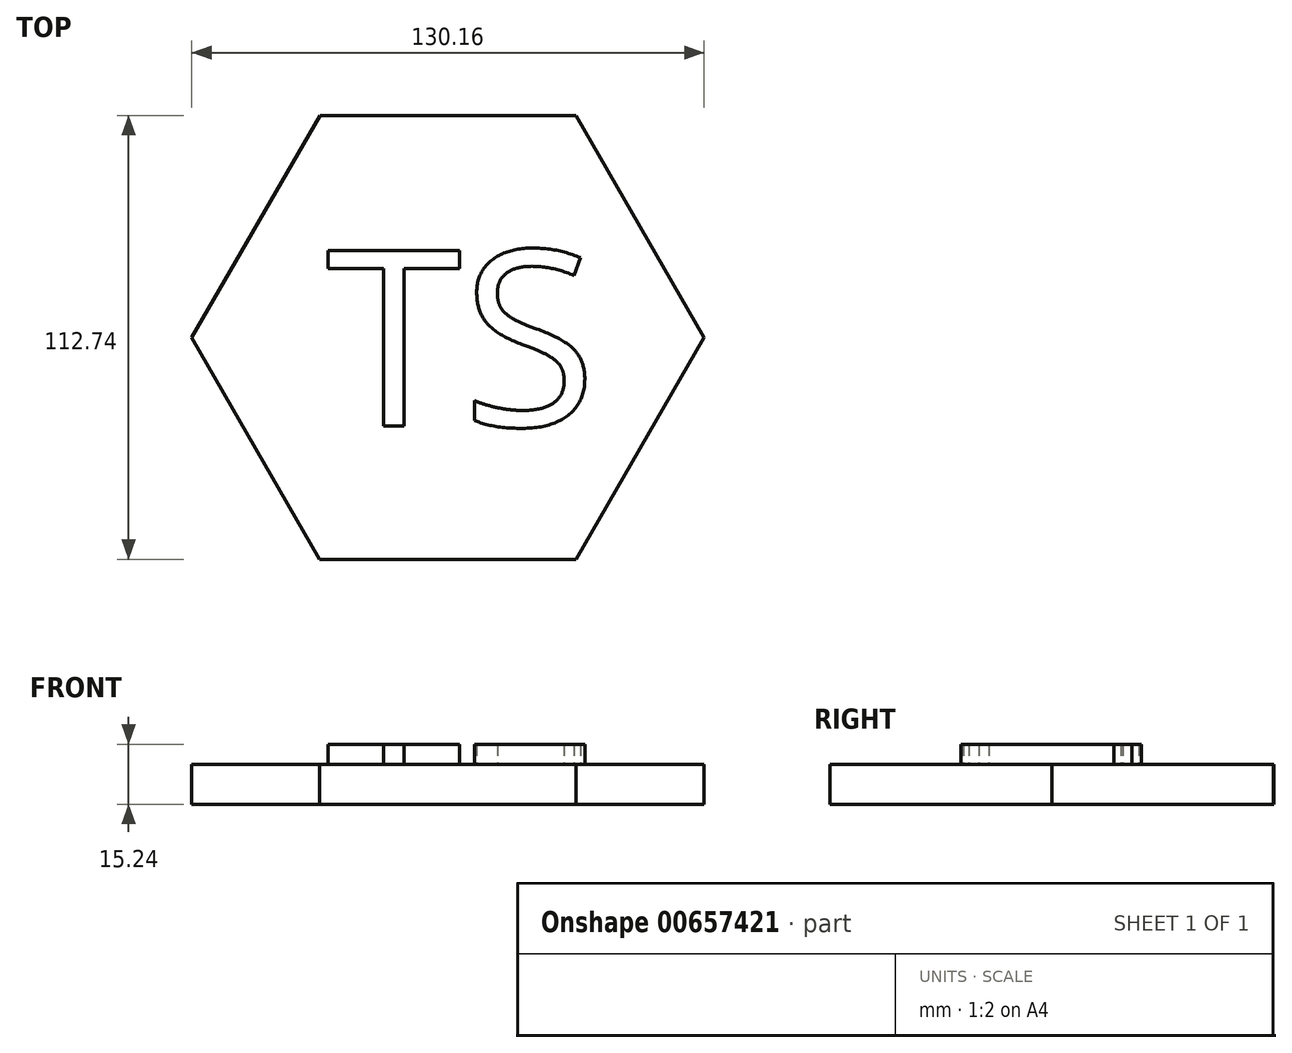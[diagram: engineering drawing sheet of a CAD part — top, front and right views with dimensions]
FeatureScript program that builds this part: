
annotation { "Feature Type Name" : "Feature", "Feature Type Description" : "" }
export const myFeature = defineFeature(function(context is Context, id is Id, definition is map)
    precondition{}
    {
        {
            var Q0;
            Q0=qCreatedBy(makeId("Top.planeOp"),FACE);
            var sketch = newSketch(context, id + "F0", { "sketchPlane" : qUnion([Q0])});
            skCircle(sketch, "E0.cCircle", {"center": v(0, 0) * mm, "radius": 56.36 * mm, "construction": true});
            skLineSegment(sketch, "E0.0", {"start": v(-32.57, -56.34) * mm, "end": v(-65.08, 0.03) * mm});
            skLineSegment(sketch, "E0.1", {"start": v(-65.08, 0.03) * mm, "end": v(-32.51, 56.37) * mm});
            skLineSegment(sketch, "E0.2", {"start": v(-32.51, 56.37) * mm, "end": v(32.57, 56.34) * mm});
            skLineSegment(sketch, "E0.3", {"start": v(32.57, 56.34) * mm, "end": v(65.08, -0.03) * mm});
            skLineSegment(sketch, "E0.4", {"start": v(65.08, -0.03) * mm, "end": v(32.51, -56.37) * mm});
            skLineSegment(sketch, "E0.5", {"start": v(32.51, -56.37) * mm, "end": v(-32.57, -56.34) * mm});
            skPoint(sketch, "E0.0.midPoint", {"position": v(-48.82, -28.16) * mm});
            skSolve(sketch);
        }
        {
            var Q0;
            Q0=makeQuery(id+"F0.imprint","IMPRINT",FACE,{"disambiguationData":[TD([[makeQuery(id+"F0.imprint","IMPRINT",EDGE,{"derivedFrom":sQuery(id+"F0.wireOp",EDGE,"E0.0")}),-1.0]])]});
            extrude(context, id + "F1", {"entities" : qUnion([Q0]), "depth" : 10.16 * mm, "offsetDistance" : 25.4 * mm});
        }
        {
            var Q0;
            Q0=qCreatedBy(makeId("Top.planeOp"),FACE);
            var sketch = newSketch(context, id + "F2", { "sketchPlane" : qUnion([Q0])});
            skText(sketch, "E1", { "text": "TS", "fontName": "OpenSans-Regular.ttf"});
            const initialGuessF2  = {"E1": [-0.031, -0.02247, 1, 0, 0.04493]};
            skSetInitialGuess(sketch, initialGuessF2);
            skSolve(sketch);
        }
        {
            var Q0;
            Q0=qCreatedBy(makeId("Top.planeOp"),FACE);
            var sketch = newSketch(context, id + "F3", { "sketchPlane" : qUnion([Q0])});
            skArc(sketch, "E2", {"start": v(32.14, 56.6) * mm, "mid": v(-0.1, 74.3) * mm, "end": v(-32.33, 56.6) * mm});
            skSolve(sketch);
        }
        {
            var Q0;
            Q0=sQuery(id+"F3.wireOp",EDGE,"E2");
            extrude(context, id + "F4", {"bodyType" : ToolBodyType.SURFACE, "surfaceEntities" : qUnion([Q0]), "depth" : 10.16 * mm, "offsetDistance" : 25.4 * mm});
        }
        {
            var Q0;
            Q0 = qSketchRegion(id + "F2", true);
            extrude(context, id + "F5", {"entities" : qUnion([Q0]), "operationType" : NewBodyOperationType.ADD, "depth" : 15.24 * mm, "offsetDistance" : 25.4 * mm});
        }
    });
